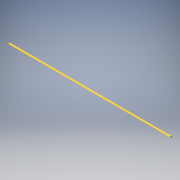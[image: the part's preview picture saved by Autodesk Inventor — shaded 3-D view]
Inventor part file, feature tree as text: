
AUTODESK INVENTOR PART (.ipt)
format: ipt  version: 2019 (Build 230136000, 136)  size: 95,232 bytes
history: native  units: in
note: dims shown in document units (in); Inventor stores cm internally (conversion verified against a paired STEP export)
features: extrude x1, sketch x1
ambient origin geometry x8: Origin, YZ Plane, XZ Plane, XY Plane, X Axis, Y Axis, Z Axis, Center Point
bodies: Solid1 (feature_tree)
feature tree (2):
  extrude  "Extrusion1"  Depth=39.3701in TaperAngle=0.0deg
  sketch  "Sketch1"  dims[d0=0.315in d1=39.3701in d2=0.0in]
